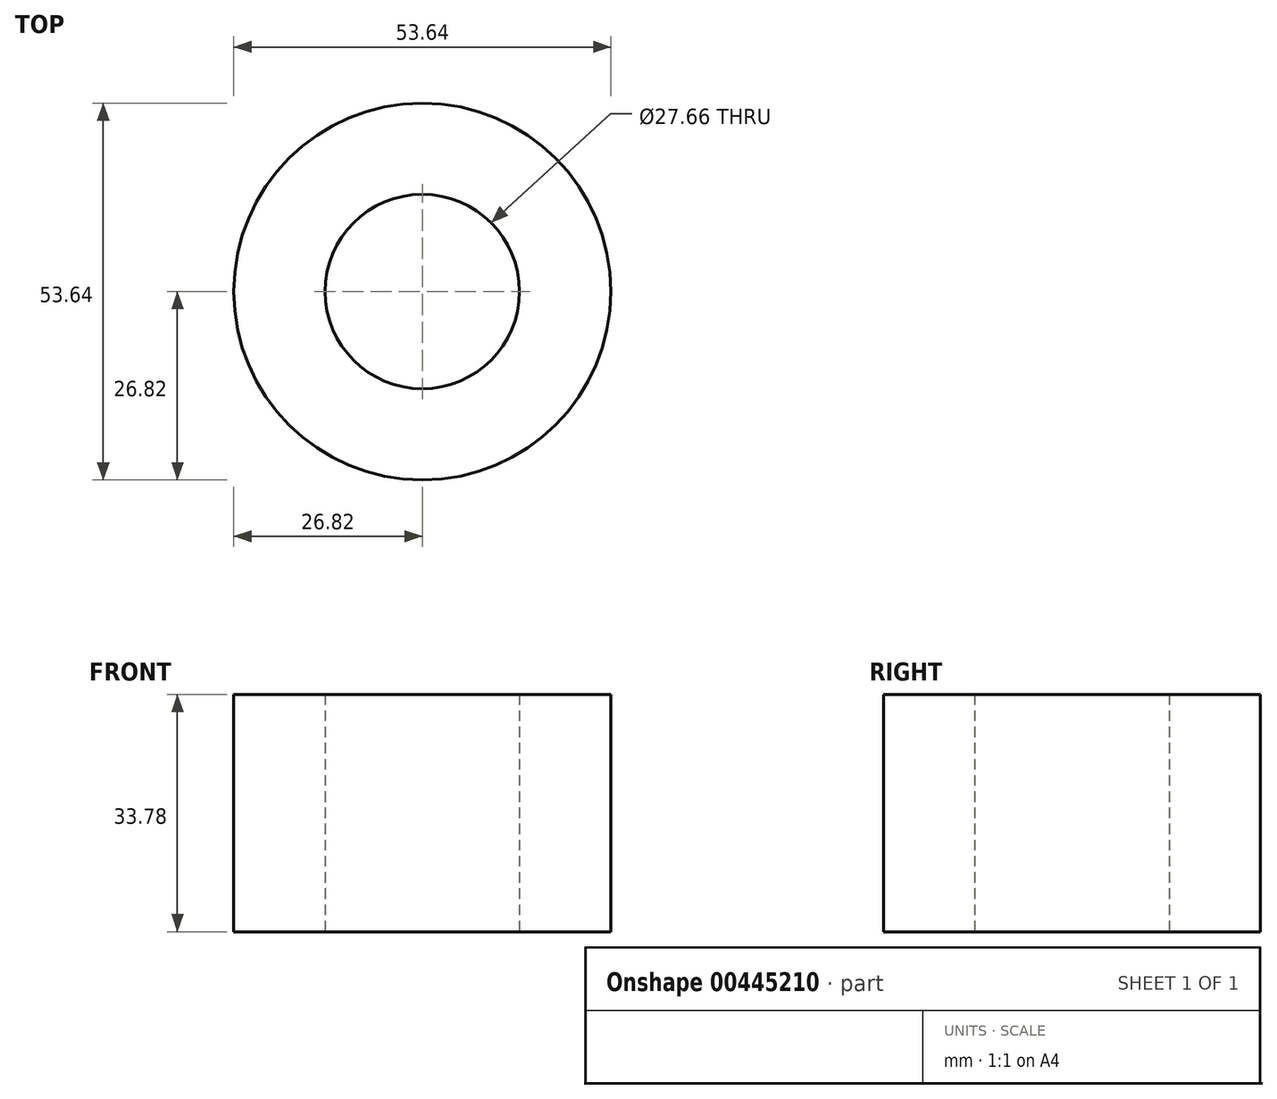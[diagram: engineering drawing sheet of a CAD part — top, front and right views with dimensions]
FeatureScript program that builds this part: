
annotation { "Feature Type Name" : "Feature", "Feature Type Description" : "" }
export const myFeature = defineFeature(function(context is Context, id is Id, definition is map)
    precondition{}
    {
        {
            var Q0;
            Q0=qCreatedBy(makeId("Top.planeOp"),FACE);
            var sketch = newSketch(context, id + "F0", { "sketchPlane" : qUnion([Q0])});
            skCircle(sketch, "E0", {"center": v(0, 0) * mm, "radius": 13.83 * mm});
            skCircle(sketch, "E1", {"center": v(0, 0) * mm, "radius": 26.82 * mm});
            skSolve(sketch);
        }
        {
            var Q0;
            Q0=makeQuery(id+"F0.imprint","IMPRINT",FACE,{"disambiguationData":[TD([[makeQuery(id+"F0.imprint","IMPRINT",EDGE,{"derivedFrom":sQuery(id+"F0.wireOp",EDGE,"E0")}),-1.0]])]});
            extrude(context, id + "F1", {"entities" : qUnion([Q0]), "depth" : 33.78 * mm});
        }
    });
